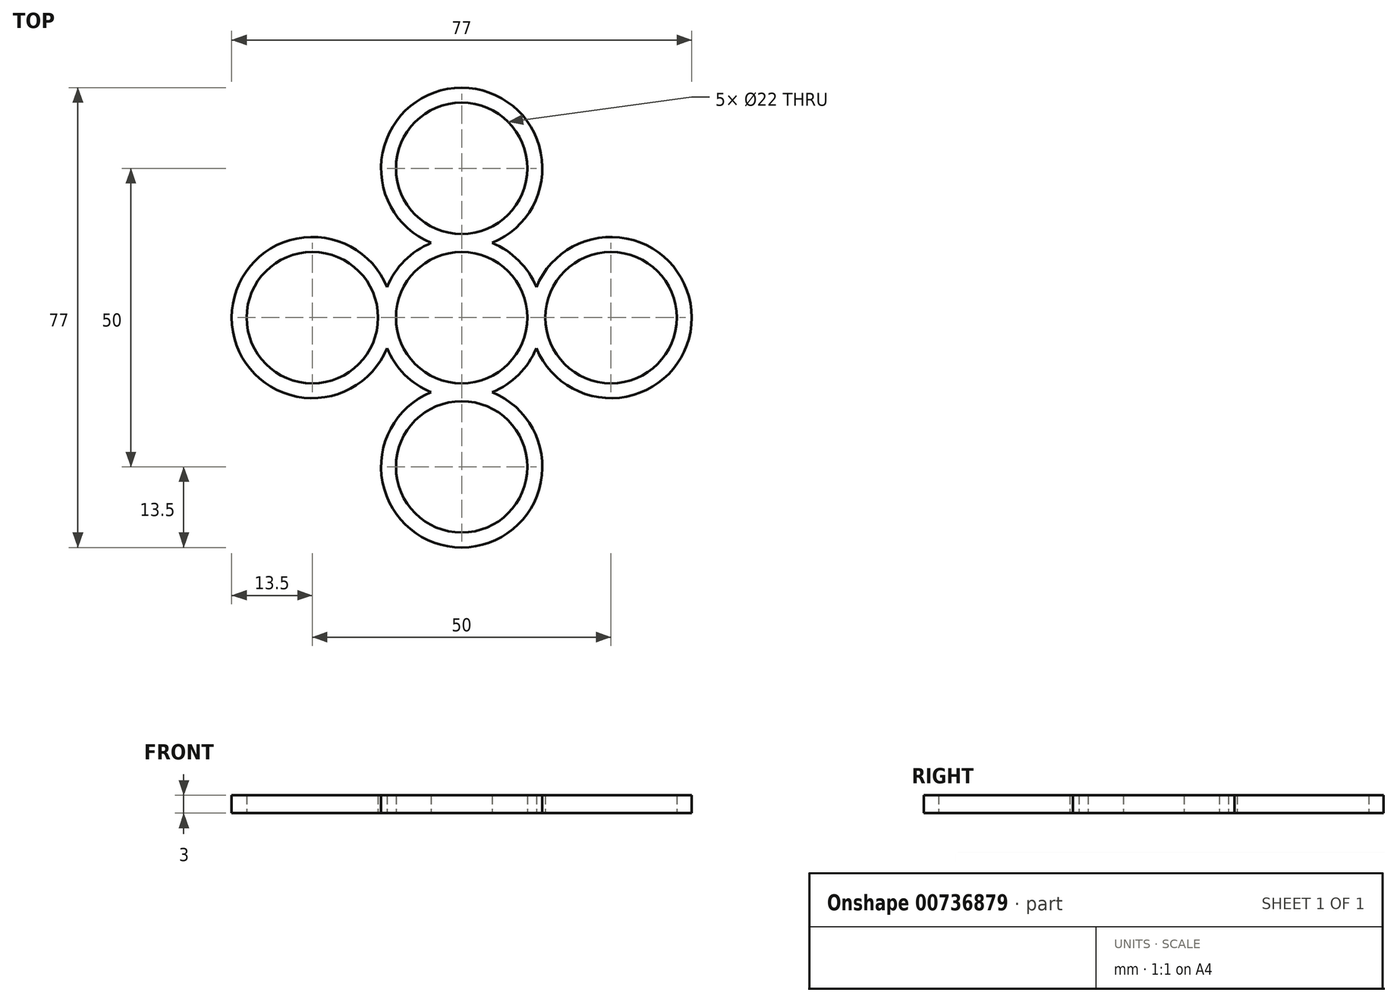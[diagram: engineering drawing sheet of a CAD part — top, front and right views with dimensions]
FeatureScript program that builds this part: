
annotation { "Feature Type Name" : "Feature", "Feature Type Description" : "" }
export const myFeature = defineFeature(function(context is Context, id is Id, definition is map)
    precondition{}
    {
        {
            var Q0;
            Q0=qCreatedBy(makeId("Top.planeOp"),FACE);
            var sketch = newSketch(context, id + "F0", { "sketchPlane" : qUnion([Q0])});
            skArc(sketch, "E0", {"start": v(7.78, 7.78) * mm, "mid": v(0, 11) * mm, "end": v(-7.78, 7.78) * mm});
            skCircle(sketch, "E1", {"center": v(0, 25) * mm, "radius": 11 * mm});
            skArc(sketch, "E2", {"start": v(-5.1, 12.5) * mm, "mid": v(-7.47, 11.24) * mm, "end": v(-9.55, 9.55) * mm});
            skArc(sketch, "E3", {"start": v(5.1, 12.5) * mm, "mid": v(0, 38.5) * mm, "end": v(-5.1, 12.5) * mm});
            skArc(sketch, "E4.trimOffspring", {"start": v(9.55, 9.55) * mm, "mid": v(7.47, 11.24) * mm, "end": v(5.1, 12.5) * mm});
            skArc(sketch, "E5.1.0", {"start": v(-12.5, 5.1) * mm, "mid": v(-38.5, 0) * mm, "end": v(-12.5, -5.1) * mm});
            skCircle(sketch, "E5.1.1", {"center": v(-25, 0) * mm, "radius": 11 * mm});
            skArc(sketch, "E5.1.2", {"start": v(-9.55, 9.55) * mm, "mid": v(-11.24, 7.47) * mm, "end": v(-12.5, 5.1) * mm});
            skArc(sketch, "E5.1.3", {"start": v(-7.78, 7.78) * mm, "mid": v(-11, 0) * mm, "end": v(-7.78, -7.78) * mm});
            skArc(sketch, "E5.1.6", {"start": v(-12.5, -5.1) * mm, "mid": v(-11.24, -7.47) * mm, "end": v(-9.55, -9.55) * mm});
            skArc(sketch, "E5.2.0", {"start": v(-5.1, -12.5) * mm, "mid": v(0, -38.5) * mm, "end": v(5.1, -12.5) * mm});
            skCircle(sketch, "E5.2.1", {"center": v(0, -25) * mm, "radius": 11 * mm});
            skArc(sketch, "E5.2.2", {"start": v(-9.55, -9.55) * mm, "mid": v(-7.47, -11.24) * mm, "end": v(-5.1, -12.5) * mm});
            skArc(sketch, "E5.2.3", {"start": v(-7.78, -7.78) * mm, "mid": v(0, -11) * mm, "end": v(7.78, -7.78) * mm});
            skArc(sketch, "E5.2.6", {"start": v(5.1, -12.5) * mm, "mid": v(7.47, -11.24) * mm, "end": v(9.55, -9.55) * mm});
            skArc(sketch, "E5.3.0", {"start": v(12.5, -5.1) * mm, "mid": v(38.5, 0) * mm, "end": v(12.5, 5.1) * mm});
            skCircle(sketch, "E5.3.1", {"center": v(25, 0) * mm, "radius": 11 * mm});
            skArc(sketch, "E5.3.2", {"start": v(9.55, -9.55) * mm, "mid": v(11.24, -7.47) * mm, "end": v(12.5, -5.1) * mm});
            skArc(sketch, "E5.3.3", {"start": v(7.78, -7.78) * mm, "mid": v(11, 0) * mm, "end": v(7.78, 7.78) * mm});
            skArc(sketch, "E5.3.6", {"start": v(12.5, 5.1) * mm, "mid": v(11.24, 7.47) * mm, "end": v(9.55, 9.55) * mm});
            skSolve(sketch);
        }
        {
            var Q0;
            Q0 = qSketchRegion(id + "F0", true);
            extrude(context, id + "F1", {"entities" : qUnion([Q0]), "depth" : 3 * mm, "offsetDistance" : 25 * mm});
        }
    });
